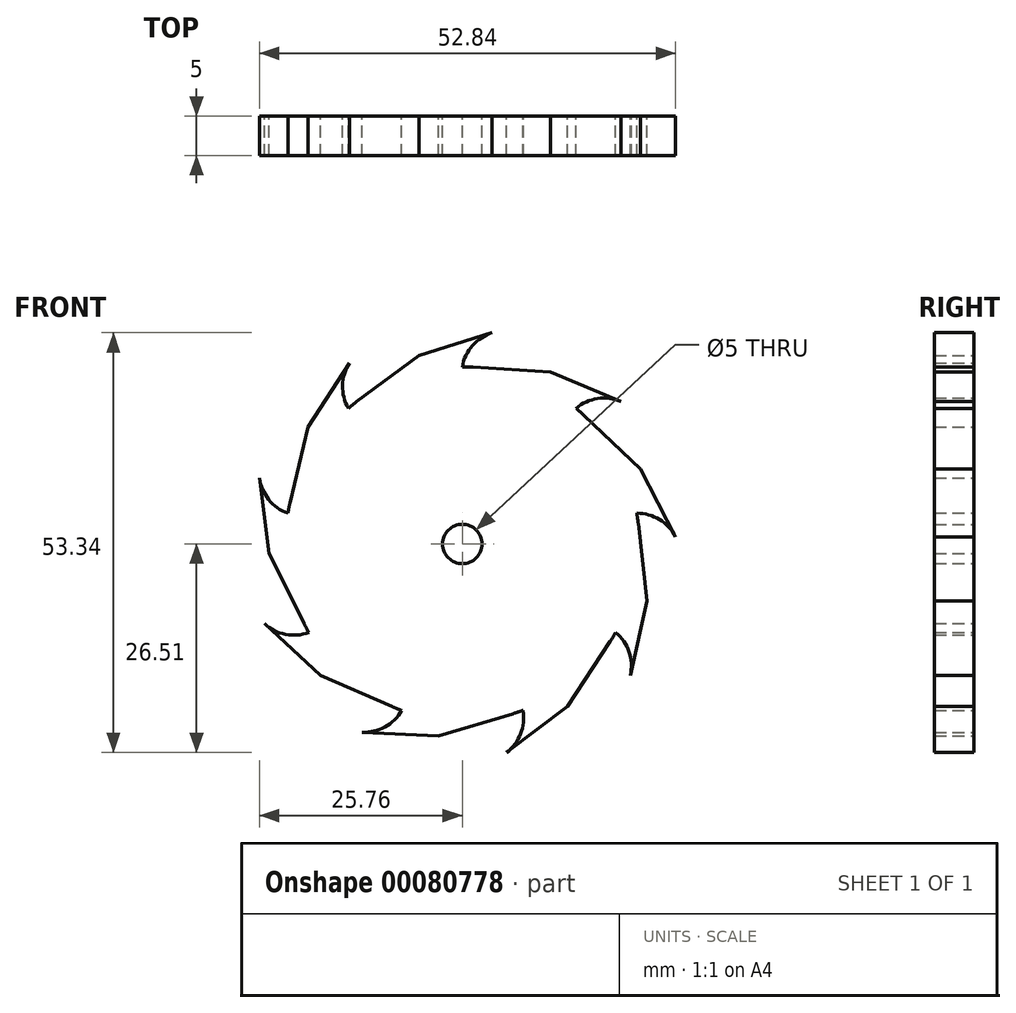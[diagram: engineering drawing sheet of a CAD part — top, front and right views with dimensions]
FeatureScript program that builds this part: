
annotation { "Feature Type Name" : "Feature", "Feature Type Description" : "" }
export const myFeature = defineFeature(function(context is Context, id is Id, definition is map)
    precondition{}
    {
        {
            var Q0;
            Q0=qCreatedBy(makeId("Front.planeOp"),FACE);
            var sketch = newSketch(context, id + "F0", { "sketchPlane" : qUnion([Q0])});
            skCircle(sketch, "E0", {"center": v(0, 0) * mm, "radius": 22.5 * mm});
            skLineSegment(sketch, "E1", {"start": v(-13.4, 18.07) * mm, "end": v(-5.48, 23.95) * mm});
            skLineSegment(sketch, "E2", {"start": v(-5.48, 23.95) * mm, "end": v(3.8, 26.83) * mm});
            skCircle(sketch, "E3", {"center": v(0, 0) * mm, "radius": 2.5 * mm});
            skArc(sketch, "E4", {"start": v(3.8, 26.83) * mm, "mid": v(1.29, 25.2) * mm, "end": v(0, 22.5) * mm});
            skLineSegment(sketch, "E5.1.0", {"start": v(-19.6, 14.83) * mm, "end": v(-14.33, 23) * mm});
            skLineSegment(sketch, "E5.1.1", {"start": v(-21.88, 5.23) * mm, "end": v(-19.6, 14.83) * mm});
            skArc(sketch, "E5.1.2", {"start": v(-14.33, 23) * mm, "mid": v(-15.21, 20.13) * mm, "end": v(-14.46, 17.24) * mm});
            skLineSegment(sketch, "E5.2.0", {"start": v(-24.54, -1.23) * mm, "end": v(-25.76, 8.4) * mm});
            skLineSegment(sketch, "E5.2.1", {"start": v(-20.12, -10.06) * mm, "end": v(-24.54, -1.23) * mm});
            skArc(sketch, "E5.2.2", {"start": v(-25.76, 8.4) * mm, "mid": v(-24.6, 5.65) * mm, "end": v(-22.16, 3.9) * mm});
            skLineSegment(sketch, "E6.1.3.0", {"start": v(-18, -16.72) * mm, "end": v(-25.13, -10.12) * mm});
            skLineSegment(sketch, "E6.3.3.0", {"start": v(-8.95, -20.64) * mm, "end": v(-18, -16.72) * mm});
            skArc(sketch, "E6.6.3.0", {"start": v(-25.13, -10.12) * mm, "mid": v(-22.47, -11.48) * mm, "end": v(-19.49, -11.25) * mm});
            skLineSegment(sketch, "E6.1.4.0", {"start": v(-3.05, -24.38) * mm, "end": v(-12.75, -23.91) * mm});
            skLineSegment(sketch, "E6.3.4.0", {"start": v(6.42, -21.57) * mm, "end": v(-3.05, -24.38) * mm});
            skArc(sketch, "E6.6.4.0", {"start": v(-12.75, -23.91) * mm, "mid": v(-9.83, -23.24) * mm, "end": v(-7.7, -21.14) * mm});
            skLineSegment(sketch, "E7.1.5.0", {"start": v(13.34, -20.63) * mm, "end": v(5.6, -26.5) * mm});
            skLineSegment(sketch, "E7.3.5.0", {"start": v(18.78, -12.4) * mm, "end": v(13.34, -20.63) * mm});
            skArc(sketch, "E7.6.5.0", {"start": v(5.6, -26.5) * mm, "mid": v(7.4, -24.12) * mm, "end": v(7.7, -21.14) * mm});
            skLineSegment(sketch, "E7.1.6.0", {"start": v(23.48, -7.23) * mm, "end": v(21.33, -16.7) * mm});
            skLineSegment(sketch, "E7.3.6.0", {"start": v(22.35, 2.57) * mm, "end": v(23.48, -7.23) * mm});
            skArc(sketch, "E7.6.6.0", {"start": v(21.33, -16.7) * mm, "mid": v(21.18, -13.72) * mm, "end": v(19.49, -11.25) * mm});
            skLineSegment(sketch, "E8.1.7.0", {"start": v(22.64, 9.55) * mm, "end": v(27.08, 0.92) * mm});
            skLineSegment(sketch, "E8.3.7.0", {"start": v(15.47, 16.34) * mm, "end": v(22.64, 9.55) * mm});
            skArc(sketch, "E8.6.7.0", {"start": v(27.08, 0.92) * mm, "mid": v(25.04, 3.1) * mm, "end": v(22.16, 3.9) * mm});
            skLineSegment(sketch, "E9.1.8.0", {"start": v(11.2, 21.87) * mm, "end": v(20.16, 18.1) * mm});
            skLineSegment(sketch, "E9.3.8.0", {"start": v(1.35, 22.46) * mm, "end": v(11.2, 21.87) * mm});
            skArc(sketch, "E9.6.8.0", {"start": v(20.16, 18.1) * mm, "mid": v(17.19, 18.48) * mm, "end": v(14.46, 17.24) * mm});
            skSolve(sketch);
        }
        {
            var Q0;
            Q0=makeQuery(id+"F0.imprint","IMPRINT",FACE,{"disambiguationData":[TD([[makeQuery(id+"F0.imprint","IMPRINT",EDGE,{"derivedFrom":sQuery(id+"F0.wireOp",EDGE,"E3")}),-1.0]])]});
            var Q1;
            {var subQ0=sQuery(id+"F0.wireOp",EDGE,"E1");Q1=makeQuery(id+"F0.imprint","IMPRINT",FACE,{"disambiguationData":[TD([[makeQuery(id+"F0.imprint","IMPRINT",EDGE,{"derivedFrom":subQ0}),-1.0]])]});}
            var Q2;
            Q2=makeQuery(id+"F0.imprint","IMPRINT",FACE,{"disambiguationData":[TD([[makeQuery(id+"F0.imprint","IMPRINT",EDGE,{"derivedFrom":sQuery(id+"F0.wireOp",EDGE,"E5.1.0")}),-1.0]])]});
            var Q3;
            Q3=makeQuery(id+"F0.imprint","IMPRINT",FACE,{"disambiguationData":[TD([[makeQuery(id+"F0.imprint","IMPRINT",EDGE,{"derivedFrom":sQuery(id+"F0.wireOp",EDGE,"E5.2.0")}),-1.0]])]});
            var Q4;
            Q4=makeQuery(id+"F0.imprint","IMPRINT",FACE,{"disambiguationData":[TD([[makeQuery(id+"F0.imprint","IMPRINT",EDGE,{"derivedFrom":sQuery(id+"F0.wireOp",EDGE,"E6.1.3.0")}),-1.0]])]});
            var Q5;
            Q5=makeQuery(id+"F0.imprint","IMPRINT",FACE,{"disambiguationData":[TD([[makeQuery(id+"F0.imprint","IMPRINT",EDGE,{"derivedFrom":sQuery(id+"F0.wireOp",EDGE,"E6.1.4.0")}),-1.0]])]});
            var Q6;
            Q6=makeQuery(id+"F0.imprint","IMPRINT",FACE,{"disambiguationData":[TD([[makeQuery(id+"F0.imprint","IMPRINT",EDGE,{"derivedFrom":sQuery(id+"F0.wireOp",EDGE,"E7.1.6.0")}),-1.0]])]});
            var Q7;
            Q7=makeQuery(id+"F0.imprint","IMPRINT",FACE,{"disambiguationData":[TD([[makeQuery(id+"F0.imprint","IMPRINT",EDGE,{"derivedFrom":sQuery(id+"F0.wireOp",EDGE,"E7.1.5.0")}),-1.0]])]});
            var Q8;
            Q8=makeQuery(id+"F0.imprint","IMPRINT",FACE,{"disambiguationData":[TD([[makeQuery(id+"F0.imprint","IMPRINT",EDGE,{"derivedFrom":sQuery(id+"F0.wireOp",EDGE,"E9.1.8.0")}),-1.0]])]});
            var Q9;
            Q9=makeQuery(id+"F0.imprint","IMPRINT",FACE,{"disambiguationData":[TD([[makeQuery(id+"F0.imprint","IMPRINT",EDGE,{"derivedFrom":sQuery(id+"F0.wireOp",EDGE,"E8.1.7.0")}),-1.0]])]});
            var Q10;
            {var subQ1=sQuery(id+"F0.wireOp",EDGE,"E2");Q10=makeQuery(id+"F0.imprint","IMPRINT",FACE,{"disambiguationData":[TD([[makeQuery(id+"F0.imprint","IMPRINT",EDGE,{"derivedFrom":subQ1}),-1.0]])]});}
            var Q11;
            {var subQ0=sQuery(id+"F0.wireOp",EDGE,"f2a72fa1-12be-4ab4-b121-d2ce65d8fceb.1.9.0");Q11=makeQuery(id+"F0.imprint","IMPRINT",FACE,{"disambiguationData":[TD([[makeQuery(id+"F0.imprint","IMPRINT",EDGE,{"derivedFrom":subQ0}),-1.0]])]});}
            extrude(context, id + "F1", {"entities" : qUnion([Q0, Q1, Q2, Q3, Q4, Q5, Q6, Q7, Q8, Q9, Q10, Q11]), "depth" : 5 * mm});
        }
    });
